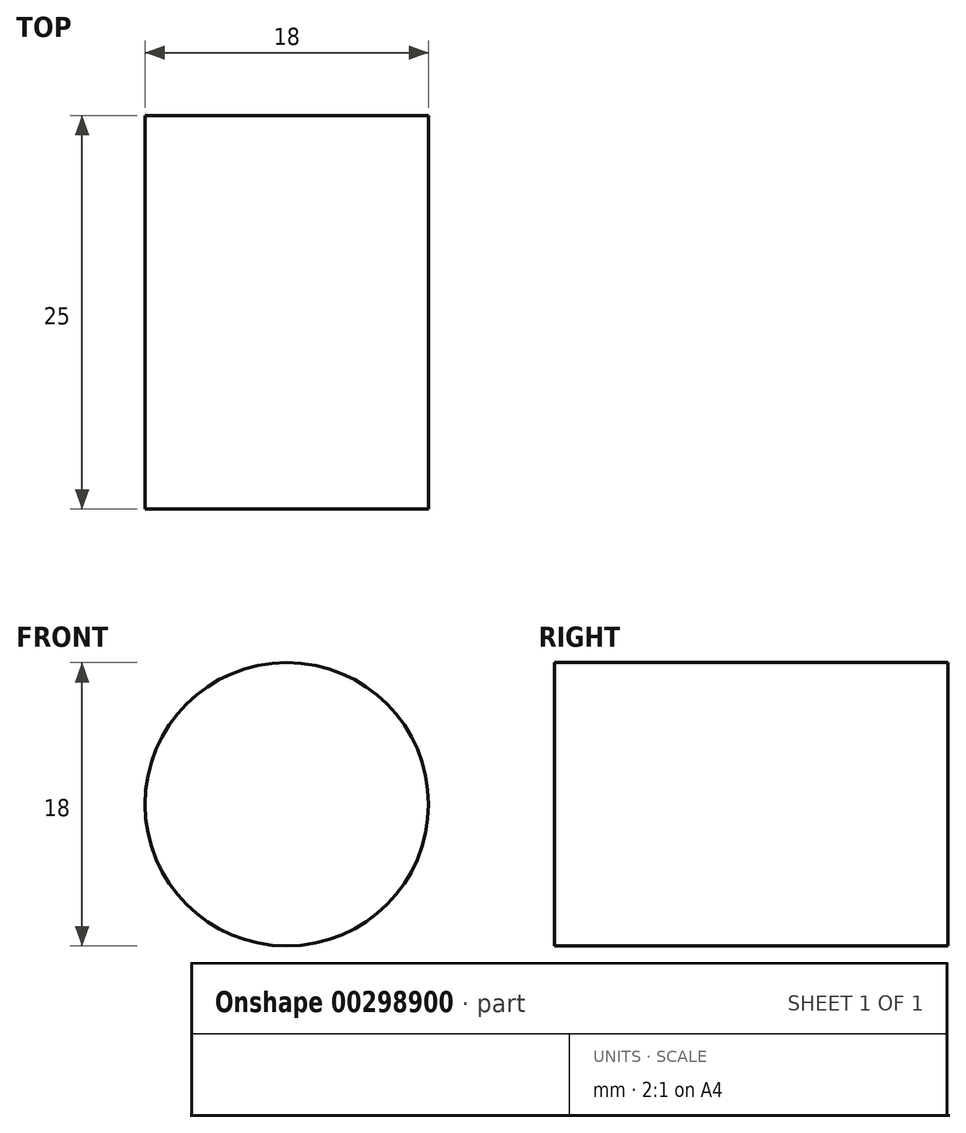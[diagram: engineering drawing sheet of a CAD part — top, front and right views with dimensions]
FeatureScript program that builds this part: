
annotation { "Feature Type Name" : "Feature", "Feature Type Description" : "" }
export const myFeature = defineFeature(function(context is Context, id is Id, definition is map)
    precondition{}
    {
        {
            var Q0;
            Q0=qCreatedBy(makeId("Front.planeOp"),FACE);
            var sketch = newSketch(context, id + "F0", { "sketchPlane" : qUnion([Q0])});
            skCircle(sketch, "E0", {"center": v(0, 0) * mm, "radius": 9 * mm});
            skSolve(sketch);
        }
        {
            var Q0;
            Q0 = qSketchRegion(id + "F0", true);
            extrude(context, id + "F1", {"entities" : qUnion([Q0]), "depth" : 25 * mm});
        }
    });
